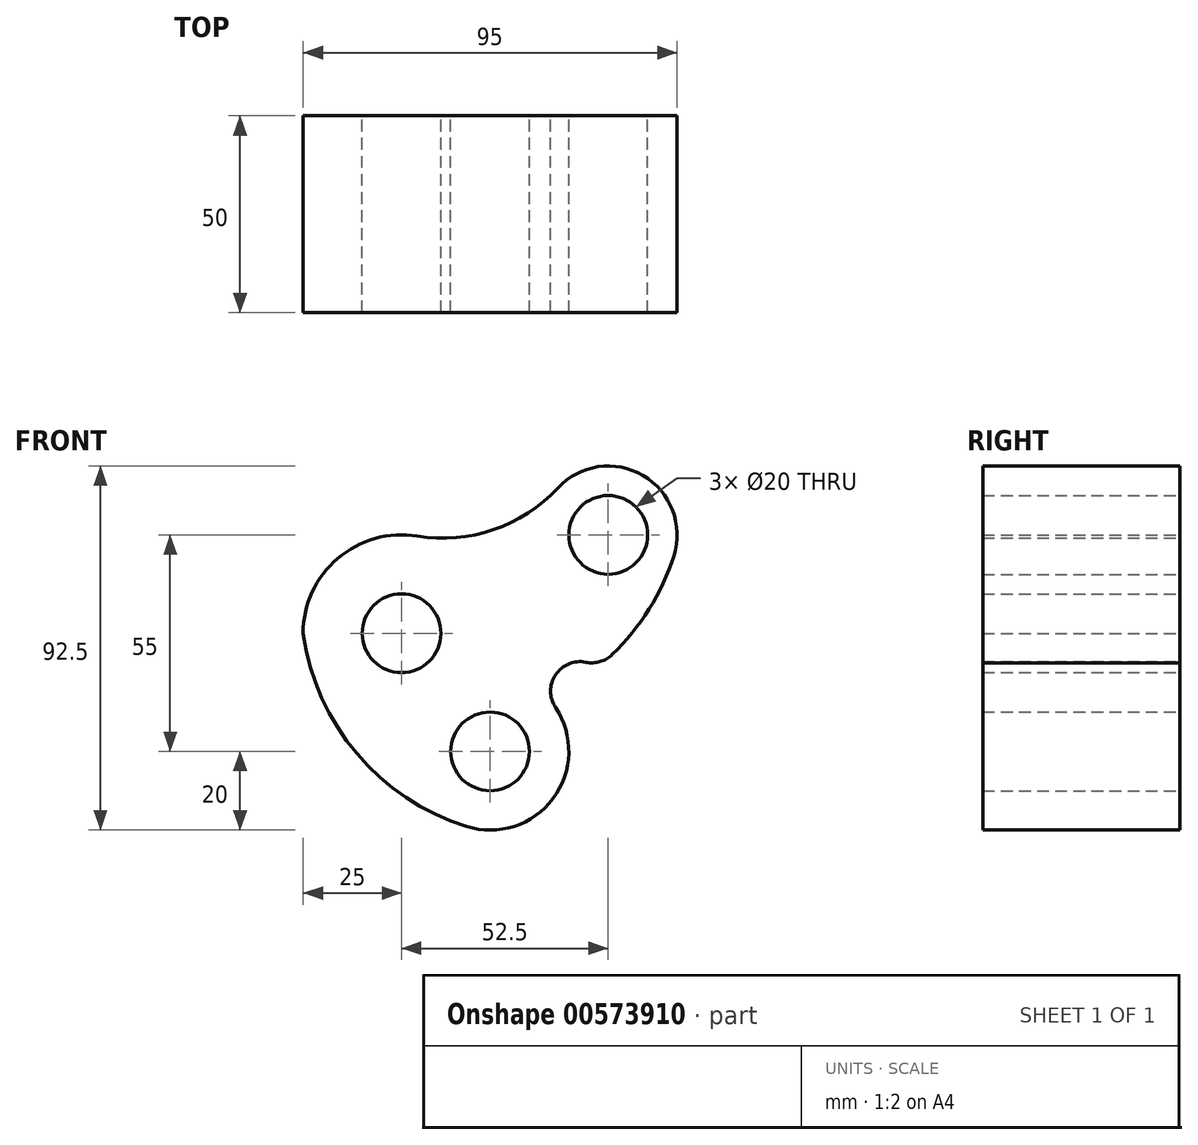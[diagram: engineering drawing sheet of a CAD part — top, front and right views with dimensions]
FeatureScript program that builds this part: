
annotation { "Feature Type Name" : "Feature", "Feature Type Description" : "" }
export const myFeature = defineFeature(function(context is Context, id is Id, definition is map)
    precondition{}
    {
        {
            var Q0;
            Q0=qCreatedBy(makeId("Front.planeOp"),FACE);
            var sketch = newSketch(context, id + "F0", { "sketchPlane" : qUnion([Q0])});
            skCircle(sketch, "E0", {"center": v(0, 0) * mm, "radius": 10 * mm});
            skCircle(sketch, "E1", {"center": v(22.5, -30) * mm, "radius": 10 * mm});
            skCircle(sketch, "E2", {"center": v(52.5, 25) * mm, "radius": 10 * mm});
            skArc(sketch, "E3", {"start": v(4, 24.68) * mm, "mid": v(-16.2, 19.04) * mm, "end": v(-25, 0) * mm});
            skArc(sketch, "E4", {"start": v(16.53, -49.09) * mm, "mid": v(38.52, -41.98) * mm, "end": v(39.12, -18.87) * mm});
            skArc(sketch, "E5", {"start": v(-25, 0) * mm, "mid": v(-11.37, -30.58) * mm, "end": v(16.53, -49.09) * mm});
            skArc(sketch, "E6", {"start": v(69.17, 19.69) * mm, "mid": v(61.33, 40.1) * mm, "end": v(39.69, 36.92) * mm});
            skArc(sketch, "E7", {"start": v(4, 24.68) * mm, "mid": v(23.38, 26.33) * mm, "end": v(39.69, 36.92) * mm});
            skArc(sketch, "E8", {"start": v(46.84, -7.35) * mm, "mid": v(50.42, -7.2) * mm, "end": v(53.52, -5.41) * mm});
            skArc(sketch, "E9", {"start": v(53.52, -5.41) * mm, "mid": v(62.92, 6.16) * mm, "end": v(69.17, 19.69) * mm});
            skArc(sketch, "E10", {"start": v(46.84, -7.35) * mm, "mid": v(39.12, -10.52) * mm, "end": v(39.12, -18.87) * mm});
            skSolve(sketch);
        }
        {
            var Q0;
            Q0=makeQuery(id+"F0.imprint","IMPRINT",FACE,{"disambiguationData":[TD([[makeQuery(id+"F0.imprint","IMPRINT",EDGE,{"derivedFrom":sQuery(id+"F0.wireOp",EDGE,"E0")}),-1.0]])]});
            extrude(context, id + "F1", {"entities" : qUnion([Q0]), "depth" : 50 * mm, "offsetDistance" : 25 * mm});
        }
    });
